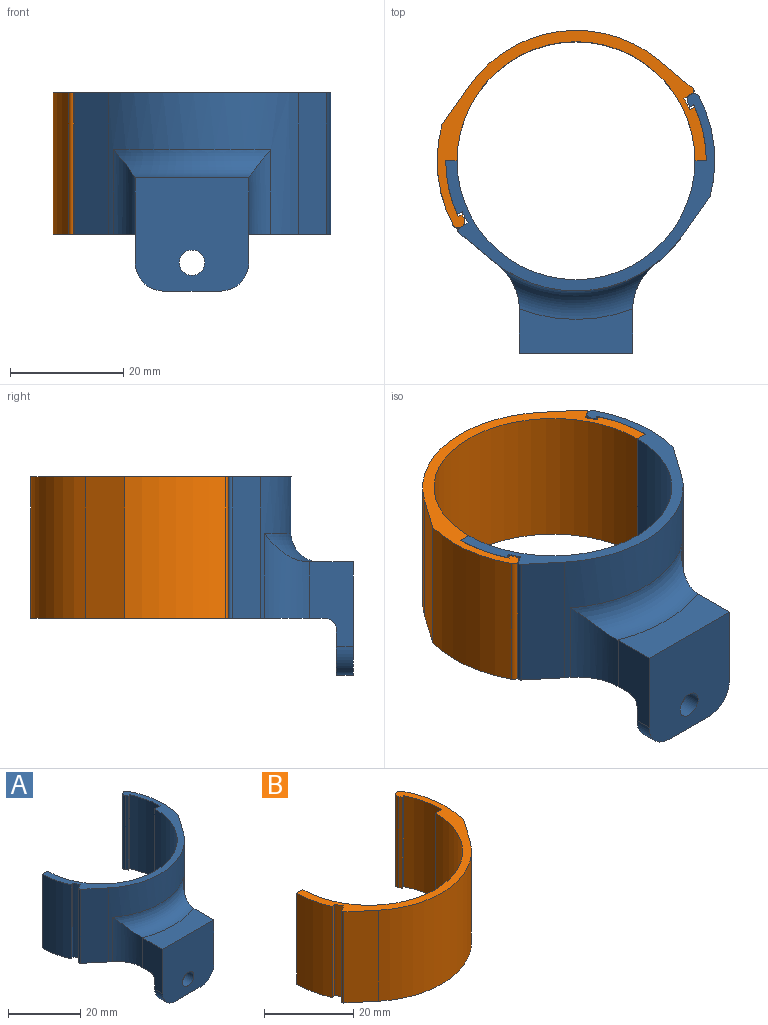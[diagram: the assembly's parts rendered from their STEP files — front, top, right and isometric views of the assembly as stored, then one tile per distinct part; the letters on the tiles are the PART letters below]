
ASSEMBLY  parts=2 mates=1
PART A: 33 faces, bbox 47.5x46x35 mm
  f0: plane 47.5x40.87mm, normal (0,0,-1), area 316.4mm2, adj f1,f2,f3,f4,f5,f6,f7,f8
  f1: cylinder r=23mm len=33.54mm, axis (0,0,-1), area 501.1mm2, adj f0,f9,f10,f16,f27,f28,f32
  f2: plane 25x2mm, normal (0,1,0), area 50mm2, adj f0,f3,f15,f16
  f3: cylinder r=21mm len=42mm, axis (0,0,-1), area 1649.3mm2, adj f0,f2,f4,f16
  f4: plane 25x2mm, normal (0,1,0), area 50mm2, adj f0,f3,f5,f16
  f5: cylinder r=23mm len=25mm, axis (0,0,-1), area 242.4mm2, adj f0,f4,f6,f16
  f6: plane 25x0.91mm, normal (0.41,-0.91,0), area 25mm2, adj f0,f5,f7,f16
  f7: cylinder r=22mm len=25mm, axis (0,0,-1), area 56.1mm2, adj f0,f6,f8,f16
  f8: plane 25x1.55mm, normal (-0.5,0.87,0), area 44.6mm2, adj f0,f7,f16,f19
  f9: plane 25x5.93mm, normal (-0.64,-0.77,0), area 193.1mm2, adj f0,f1,f16,f19
  f10: plane 25x6.9mm, normal (0.82,-0.58,0), area 211mm2, adj f0,f1,f11,f16
  f11: cylinder r=24.5mm len=25mm, axis (0,0,-1), area 455mm2, adj f0,f10,f16,f18
  f12: plane 25x0.22mm, normal (-0.5,0.87,0), area 6.3mm2, adj f0,f16,f17,f18
  f13: cylinder r=22.25mm len=25mm, axis (0,0,-1), area 21.5mm2, adj f0,f14,f16,f17
  f14: plane 25x0.68mm, normal (0.43,-0.9,0), area 18.8mm2, adj f0,f13,f15,f16
  f15: cylinder r=23mm len=25mm, axis (0,0,-1), area 254.1mm2, adj f0,f2,f14,f16
  f16: plane 47.5x34.87mm, normal (0,0,1), area 172.8mm2, adj f1,f2,f3,f4,f5,f6,f7,f8
  f17: cylinder r=1mm len=25mm, axis (0,0,-1), area 38.2mm2, adj f0,f12,f13,f16
  f18: cylinder r=1mm len=25mm, axis (0,0,-1), area 40.3mm2, adj f0,f11,f12,f16
  f19: cylinder r=0.5mm len=25mm, axis (0,0,1), area 24mm2, adj f0,f8,f9,f16
  f20: plane 15x7.75mm, normal (-1,0,0), area 93.4mm2, adj f0,f21,f23,f24,f27,f29,f30
  f21: plane 20x20mm, normal (0,-1,0), area 373.4mm2, adj f20,f22,f23,f25,f26,f30,f31
  f22: plane 15x7.75mm, normal (1,0,0), area 93.4mm2, adj f0,f21,f23,f24,f28,f29,f31
  f23: plane 20x7.85mm, normal (0,0,1), area 132.1mm2, adj f20,f21,f22,f27,f28,f32
  f24: plane 20x8mm, normal (0,1,0), area 133.4mm2, adj f20,f22,f25,f26,f29,f30,f31
  f25: plane 10x3mm, normal (0,0,-1), area 30mm2, adj f21,f24,f30,f31
  f26: cylinder r=2.25mm len=4.5mm, axis (0,1,0), area 42.4mm2, adj f21,f24
  f27: cylinder r=10mm len=15mm, axis (0,0,-1), area 108.8mm2, adj f0,f1,f20,f23,f32
  f28: cylinder r=10mm len=15mm, axis (0,0,-1), area 108.8mm2, adj f0,f1,f22,f23,f32
  f29: cylinder r=2mm len=20mm, axis (-1,0,0), area 62.8mm2, adj f0,f20,f22,f24
  f30: cylinder r=5mm len=5mm, axis (0,-1,0), area 23.6mm2, adj f20,f21,f24,f25
  f31: cylinder r=5mm len=5mm, axis (0,1,0), area 23.6mm2, adj f21,f22,f24,f25
  f32: torus R=28mm, axis (0,0,1), area 185.8mm2, adj f1,f23,f27,f28
PART B: 20 faces, bbox 47.5x34.9x25 mm
  f0: plane 25x2mm, normal (0,1,0), area 50mm2, adj f1,f14,f15,f16
  f1: cylinder r=21mm len=42mm, axis (0,0,-1), area 1649.3mm2, adj f0,f2,f15,f16
  f2: plane 25x2mm, normal (0,1,0), area 50mm2, adj f1,f3,f15,f16
  f3: cylinder r=23mm len=25mm, axis (0,0,-1), area 242.4mm2, adj f2,f4,f15,f16
  f4: plane 25x0.91mm, normal (0.41,-0.91,0), area 25mm2, adj f3,f5,f15,f16
  f5: cylinder r=22mm len=25mm, axis (0,0,-1), area 56.1mm2, adj f4,f6,f15,f16
  f6: plane 25x1.55mm, normal (-0.5,0.87,0), area 44.6mm2, adj f5,f15,f16,f19
  f7: plane 25x5.93mm, normal (-0.64,-0.77,0), area 193.1mm2, adj f8,f15,f16,f19
  f8: cylinder r=23mm len=33.54mm, axis (0,0,-1), area 950.3mm2, adj f7,f9,f15,f16
  f9: plane 25x6.9mm, normal (0.82,-0.58,0), area 211mm2, adj f8,f10,f15,f16
  f10: cylinder r=24.5mm len=25mm, axis (0,0,-1), area 455mm2, adj f9,f15,f16,f18
  f11: plane 25x0.22mm, normal (-0.5,0.87,0), area 6.3mm2, adj f15,f16,f17,f18
  f12: cylinder r=22.25mm len=25mm, axis (0,0,-1), area 21.5mm2, adj f13,f15,f16,f17
  f13: plane 25x0.68mm, normal (0.43,-0.9,0), area 18.8mm2, adj f12,f14,f15,f16
  f14: cylinder r=23mm len=25mm, axis (0,0,-1), area 254.1mm2, adj f0,f13,f15,f16
  f15: plane 47.5x34.87mm, normal (0,0,1), area 172.8mm2, adj f0,f1,f2,f3,f4,f5,f6,f7
  f16: plane 47.5x34.87mm, normal (0,0,-1), area 172.8mm2, adj f0,f1,f2,f3,f4,f5,f6,f7
  f17: cylinder r=1mm len=25mm, axis (0,0,-1), area 38.2mm2, adj f11,f12,f15,f16
  f18: cylinder r=1mm len=25mm, axis (0,0,-1), area 40.3mm2, adj f10,f11,f15,f16
  f19: cylinder r=0.5mm len=25mm, axis (0,0,1), area 24mm2, adj f6,f7,f15,f16
PLACE A t=(-7.34,-6.68,-2.11)mm
PLACE B rot(axis=(0,0,1),180deg) t=(42.66,-6.68,-2.11)mm
MATE planar B.f1 <-> A.f3  axis (0,0,1) through (-7.34,-6.68,22.89)mm
